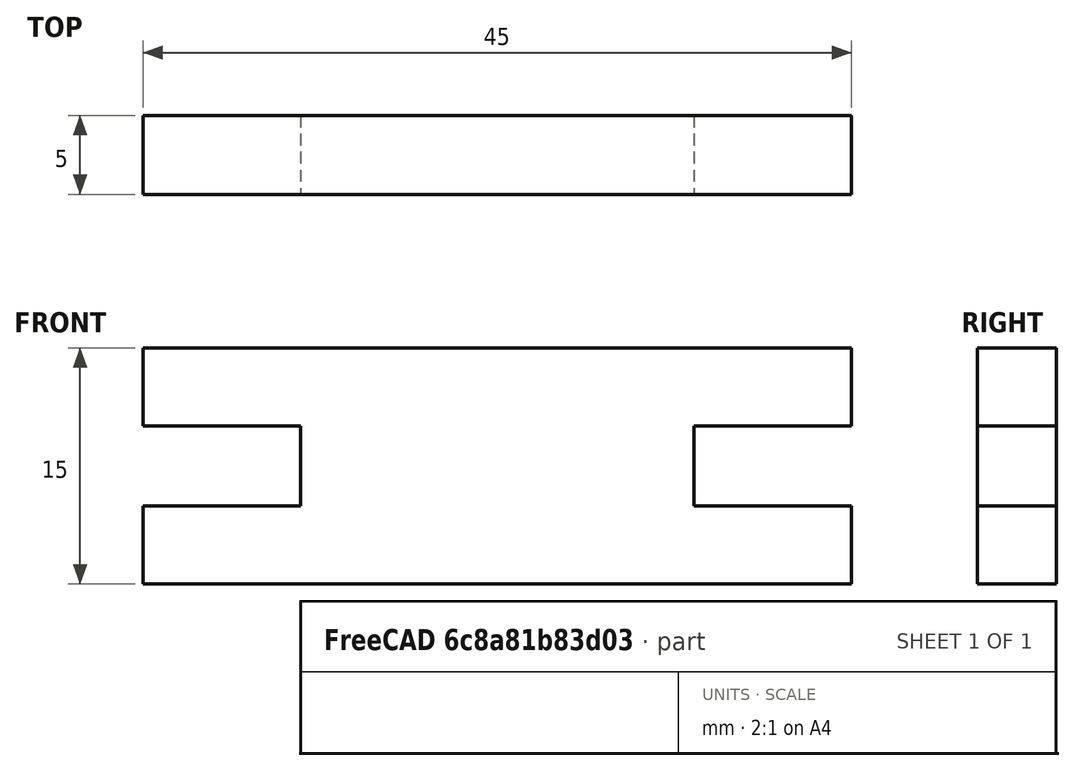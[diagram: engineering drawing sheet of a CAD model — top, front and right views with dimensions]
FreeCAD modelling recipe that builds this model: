
FCSTD DOCUMENT  (FreeCAD 1.0R39319 (Git))
Label: X Axis Far Leg Short Version
License: All rights reserved
LicenseURL: https://en.wikipedia.org/wiki/All_rights_reserved
objects: PartDesign::CoordinateSystem×2, Sketcher::SketchObject×1, PartDesign::Pad×1, PartDesign::Body×1, App::Part×1
note: 8 computed .brp shape members not serialized (recipe doc carries the construction recipe); baked Part::Feature solids carry a one-line shape summary decoded from their .brp

FEATURE [Sketcher::SketchObject] Sketch
  ArcFitTolerance = 1e-06
  AttachmentSupport = -> [XZ_Plane001]
  FullyConstrained = true
  MakeInternals = false
  MapMode = 5
  Placement = pos=(0,0,0) rot=(1,0,0;1.5708rad)
  sketch-geometry (14):
    g0: LineSegment StartX=0 StartY=7.5 StartZ=0 EndX=0 EndY=2.55 EndZ=0
    g1: LineSegment StartX=0 StartY=-7.5 StartZ=0 EndX=45 EndY=-7.5 EndZ=0
    g2: LineSegment StartX=45 StartY=-7.5 StartZ=0 EndX=45 EndY=-2.55 EndZ=0
    g3: LineSegment StartX=45 StartY=7.5 StartZ=0 EndX=0 EndY=7.5 EndZ=0
    g4: LineSegment StartX=0 StartY=2.55 StartZ=0 EndX=10 EndY=2.55 EndZ=0
    g5: LineSegment StartX=10 StartY=2.55 StartZ=0 EndX=10 EndY=-2.55 EndZ=0
    g6: LineSegment StartX=10 StartY=-2.55 StartZ=0 EndX=0 EndY=-2.55 EndZ=0
    g7: LineSegment StartX=0 StartY=-2.55 StartZ=0 EndX=0 EndY=-7.5 EndZ=0
    g8: GeomPoint [constr] X=10 Y=0 Z=0
    g9: LineSegment StartX=45 StartY=2.55 StartZ=0 EndX=35 EndY=2.55 EndZ=0
    g10: LineSegment StartX=35 StartY=2.55 StartZ=0 EndX=35 EndY=-2.55 EndZ=0
    g11: LineSegment StartX=35 StartY=-2.55 StartZ=0 EndX=45 EndY=-2.55 EndZ=0
    g12: LineSegment StartX=45 StartY=2.55 StartZ=0 EndX=45 EndY=7.5 EndZ=0
    g13: GeomPoint [constr] X=35 Y=-1e-16 Z=0
  constraints (40):
    c: Coincident(g7,g1)
    c: Coincident(g1,g2)
    c: Coincident(g12,g3)
    c: Coincident(g3,g0)
    c: Vertical(g0)
    c: Vertical(g2)
    c: Horizontal(g1)
    c: Horizontal(g3)
    c: DistanceX(g3,g3) = 45
    c: Distance(g2,g12) = 15
    c: Horizontal(g4)
    c: Coincident(g4,g5)
    c: Vertical(g5)
    c: Coincident(g5,g6)
    c: PointOnObject(g6,g7)
    c: Horizontal(g6)
    c: Coincident(g0,g4)
    c: PointOnObject(g7,g6)
    c: DistanceX(g4,g4) = 10
    c: Symmetric(g5,g5,g8)
    c: Distance(g8,g3) = 7.5
    c: Distance(g6,g4) = 5.1
    c: PointOnObject(g0,g7)
    c: Vertical(g7)
    c: PointOnObject(g9,g12)
    c: Horizontal(g9)
    c: Coincident(g9,g10)
    c: Vertical(g10)
    c: Coincident(g10,g11)
    c: Horizontal(g11)
    c: Coincident(g2,g11)
    c: PointOnObject(g12,g9)
    c: DistanceX(g9,g9) = 10
    c: Vertical(g12)
    c: Distance(g11,g9) = 5.1
    c: PointOnObject(g9,g2)
    c: Symmetric(g10,g10,g13)
    c: Distance(g13,g3) = 7.5
    c: PointOnObject(g8,g-1)
    c: PointOnObject(g0,g-2)
FEATURE [PartDesign::Pad] Pad
  Direction = (0,-1,2e-16)
  Length = 5
  Length2 = 10
  Midplane = true
  Placement = pos=(0,0,0) rot=(1,0,0;1.5708rad)
  Profile = -> Sketch
  ReferenceAxis = -> Sketch [N_Axis]
  Refine = true
  Suppressed = false
  Type = 0
FEATURE [PartDesign::Body] Body  label="X Axis Far Leg Short Version001"
  AllowCompound = false
  Group = -> [Sketch,Pad]
  Origin = -> Origin001
  Tip = -> Pad
FEATURE [PartDesign::CoordinateSystem] LCS_1
  AttacherType = Attacher::AttachEngine3D
  AttachmentOffset = pos=(10,0,0) rot=(0,0,1;0rad)
  AttachmentSupport = -> [XY_Plane001]
  MapMode = 2
  Placement = pos=(10,0,0) rot=(0,0,1;0rad)
FEATURE [PartDesign::CoordinateSystem] LCS_2
  AttacherType = Attacher::AttachEngine3D
  AttachmentOffset = pos=(35,0,0) rot=(0,0,1;0rad)
  AttachmentSupport = -> [XY_Plane001]
  MapMode = 2
  Placement = pos=(35,0,0) rot=(0,0,1;0rad)
FEATURE [App::Part] Part  label="X Axis Far Leg Short Version"
  Group = -> [Body,LCS_1,LCS_2]
  Origin = -> Origin
